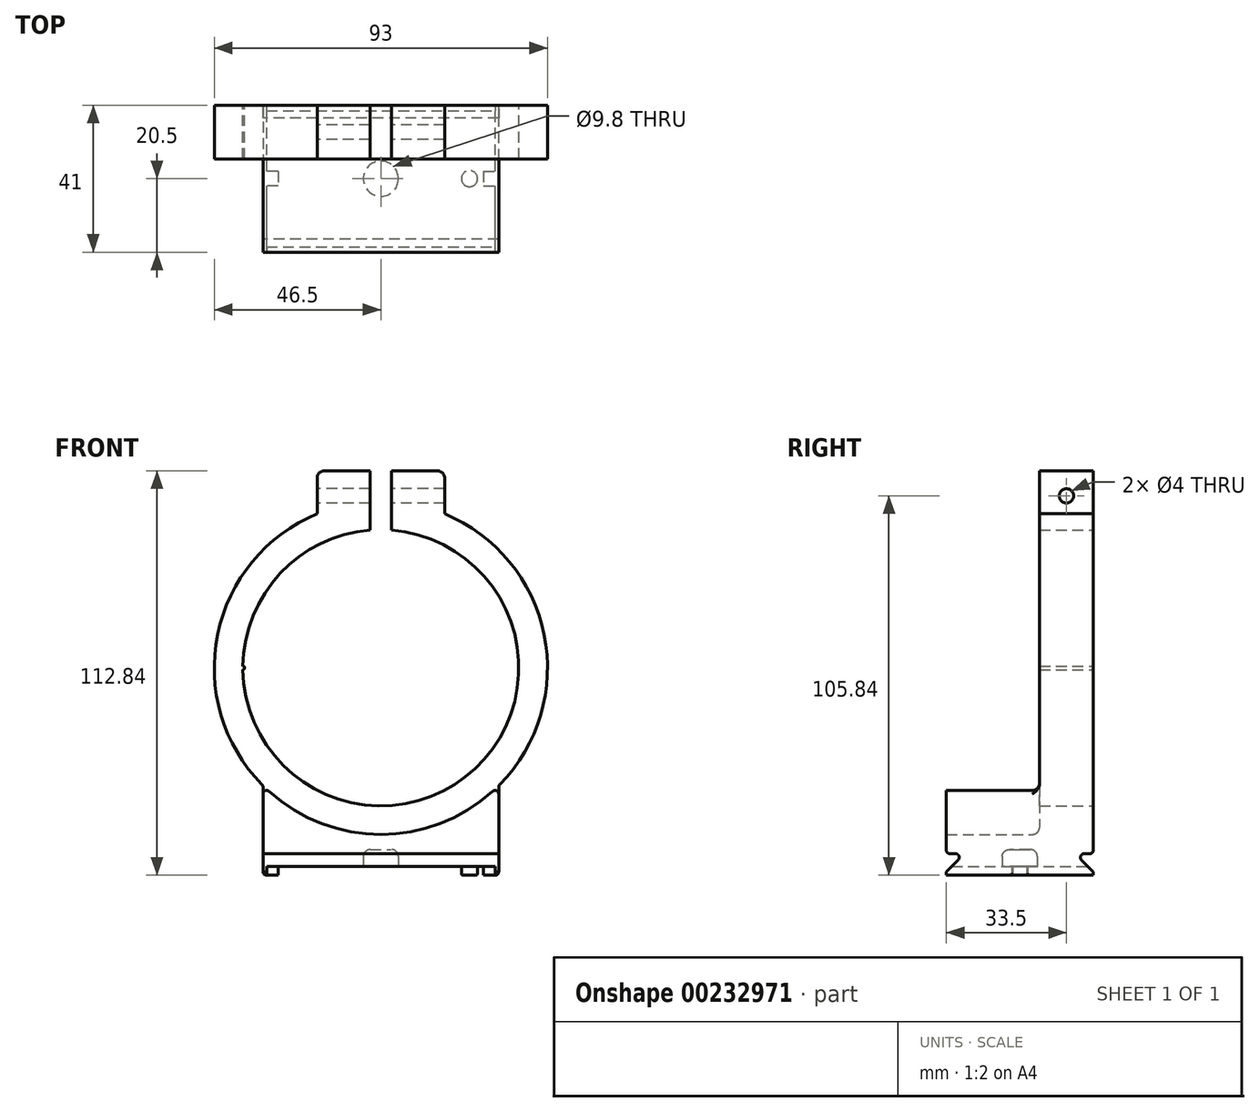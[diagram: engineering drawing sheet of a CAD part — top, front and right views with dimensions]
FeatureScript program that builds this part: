
annotation { "Feature Type Name" : "Feature", "Feature Type Description" : "" }
export const myFeature = defineFeature(function(context is Context, id is Id, definition is map)
    precondition{}
    {
        {
            var Q0;
            Q0=qCreatedBy(makeId("Front.planeOp"),FACE);
            var sketch = newSketch(context, id + "F0", { "sketchPlane" : qUnion([Q0])});
            skLineSegment(sketch, "E0", {"start": v(0, 0) * mm, "end": v(-32.88, -32.88) * mm, "construction": true});
            skLineSegment(sketch, "E1.MirrorCS", {"start": v(0, 0) * mm, "end": v(32.88, -32.88) * mm, "construction": true});
            skLineSegment(sketch, "E2", {"start": v(0, 0) * mm, "end": v(0, -46.5) * mm, "construction": true});
            skLineSegment(sketch, "E3.top", {"start": v(-32.88, -57.88) * mm, "end": v(32.88, -57.88) * mm});
            skLineSegment(sketch, "E3.left", {"start": v(-32.88, -32.88) * mm, "end": v(-32.88, -57.88) * mm});
            skLineSegment(sketch, "E3.right", {"start": v(32.88, -32.88) * mm, "end": v(32.88, -57.88) * mm});
            skLineSegment(sketch, "E4.MirrorCS", {"start": v(0, 0) * mm, "end": v(32.88, 32.88) * mm, "construction": true});
            skLineSegment(sketch, "E5.MirrorCS", {"start": v(0, 0) * mm, "end": v(-32.88, 32.88) * mm, "construction": true});
            skLineSegment(sketch, "E6", {"start": v(0, 0) * mm, "end": v(17.8, 42.96) * mm, "construction": true});
            skLineSegment(sketch, "E7.MirrorCS", {"start": v(0, 0) * mm, "end": v(-17.8, 42.96) * mm, "construction": true});
            skLineSegment(sketch, "E8.top", {"start": v(-15.8, 54.96) * mm, "end": v(-3, 54.96) * mm});
            skLineSegment(sketch, "E8.left", {"start": v(-17.8, 42.96) * mm, "end": v(-17.8, 52.96) * mm});
            skLineSegment(sketch, "E8.right", {"start": v(17.8, 42.96) * mm, "end": v(17.8, 52.96) * mm});
            skPoint(sketch, "E9.visualSharp", {"position": v(-17.8, 54.96) * mm});
            skArc(sketch, "E9.filletArc", {"start": v(-15.8, 54.96) * mm, "mid": v(-17.2, 54.37) * mm, "end": v(-17.8, 52.96) * mm});
            skPoint(sketch, "E10.visualSharp", {"position": v(17.8, 54.96) * mm});
            skArc(sketch, "E10.filletArc", {"start": v(17.8, 52.96) * mm, "mid": v(17.2, 54.37) * mm, "end": v(15.8, 54.96) * mm});
            skPoint(sketch, "E11", {"position": v(-3, 38.38) * mm});
            skPoint(sketch, "E12.MirrorP", {"position": v(3, 38.38) * mm});
            skLineSegment(sketch, "E13", {"start": v(-3, 38.38) * mm, "end": v(-3, 46.4) * mm});
            skLineSegment(sketch, "E14", {"start": v(3, 38.38) * mm, "end": v(3, 46.4) * mm});
            skLineSegment(sketch, "E15", {"start": v(0.05, 38.5) * mm, "end": v(0.05, 38.5) * mm});
            skArc(sketch, "E16", {"start": v(-3, 38.38) * mm, "mid": v(0, -38.5) * mm, "end": v(3, 38.38) * mm});
            skLineSegment(sketch, "E17", {"start": v(3, 54.96) * mm, "end": v(15.8, 54.96) * mm});
            skLineSegment(sketch, "E18", {"start": v(-3, 46.4) * mm, "end": v(-3, 54.96) * mm});
            skLineSegment(sketch, "E19", {"start": v(3, 46.4) * mm, "end": v(3, 54.96) * mm});
            skArc(sketch, "E20", {"start": v(-3, 46.4) * mm, "mid": v(0, -46.5) * mm, "end": v(3, 46.4) * mm});
            skArc(sketch, "E21", {"start": v(-38.5, -0.5) * mm, "mid": v(-38, 0) * mm, "end": v(-38.5, 0.5) * mm});
            skArc(sketch, "E22.MirrorCS", {"start": v(-0.5, -38.5) * mm, "mid": v(0, -38) * mm, "end": v(0.5, -38.5) * mm});
            skArc(sketch, "E23.MirrorCS", {"start": v(38.5, -0.5) * mm, "mid": v(38, 0) * mm, "end": v(38.5, 0.5) * mm});
            skSolve(sketch);
        }
        {
            var Q0;
            Q0=makeQuery(id+"F0.imprint","IMPRINT",FACE,{"disambiguationData":[TD([[makeQuery(id+"F0.imprint","IMPRINT",EDGE,{"derivedFrom":sQuery(id+"F0.wireOp",EDGE,"1u5II1qU-nMGl-KZTy-Vj3Y-kYBSh77GBjj7")}),-1.0]])]});
            var Q1;
            {var subQ0=sQuery(id+"F0.wireOp",EDGE,"E8.left");Q1=makeQuery(id+"F0.imprint","IMPRINT",FACE,{"disambiguationData":[TD([[makeQuery(id+"F0.imprint","IMPRINT",EDGE,{"derivedFrom":subQ0}),-1.0]])]});}
            var Q2;
            {var subQ0=sQuery(id+"F0.wireOp",EDGE,"E8.right");Q2=makeQuery(id+"F0.imprint","IMPRINT",FACE,{"disambiguationData":[TD([[makeQuery(id+"F0.imprint","IMPRINT",EDGE,{"derivedFrom":subQ0}),1.0]])]});}
            var Q3;
            {var subQ2=sQuery(id+"F0.wireOp",EDGE,"E13");Q3=makeQuery(id+"F0.imprint","IMPRINT",FACE,{"disambiguationData":[TD([[makeQuery(id+"F0.imprint","IMPRINT",EDGE,{"derivedFrom":subQ2}),1.0]])]});}
            var Q4;
            {var subQ0=sQuery(id+"F0.wireOp",EDGE,"E21");Q4=makeQuery(id+"F0.imprint","IMPRINT",FACE,{"disambiguationData":[TD([[makeQuery(id+"F0.imprint","IMPRINT",EDGE,{"derivedFrom":subQ0}),1.0]])]});}
            var Q5;
            {var subQ0=sQuery(id+"F0.wireOp",EDGE,"E22.MirrorCS");Q5=makeQuery(id+"F0.imprint","IMPRINT",FACE,{"disambiguationData":[TD([[makeQuery(id+"F0.imprint","IMPRINT",EDGE,{"derivedFrom":subQ0}),-1.0]])]});}
            var Q6;
            {var subQ0=sQuery(id+"F0.wireOp",EDGE,"E23.MirrorCS");Q6=makeQuery(id+"F0.imprint","IMPRINT",FACE,{"disambiguationData":[TD([[makeQuery(id+"F0.imprint","IMPRINT",EDGE,{"derivedFrom":subQ0}),-1.0]])]});}
            var Q7;
            Q7=makeQuery(id+"F0.imprint","IMPRINT",FACE,{"disambiguationData":[TD([[makeQuery(id+"F0.imprint","IMPRINT",EDGE,{"derivedFrom":sQuery(id+"F0.wireOp",EDGE,"E3.top")}),1.0]])]});
            extrude(context, id + "F1", {"entities" : qUnion([Q0, Q1, Q2, Q3, Q4, Q5, Q6, Q7]), "endBound" : BoundingType.SYMMETRIC, "depth" : 15 * mm});
        }
        {
            var Q0;
            Q0=makeQuery(id+"F1.opExtrude","SWEPT_FACE",FACE,{"disambiguationData":[OSD([sQuery(id+"F0.wireOp",EDGE,"E8.left")])]});
            var sketch = newSketch(context, id + "F2", { "sketchPlane" : qUnion([Q0])});
            skPoint(sketch, "E24", {"position": v(0, 47.96) * mm});
            skPoint(sketch, "E24.positionSnap0", {"position": v(-7.5, 47.96) * mm});
            skPoint(sketch, "E25", {"position": v(7.5, 47.96) * mm});
            skLineSegment(sketch, "E26", {"start": v(-7.5, 47.96) * mm, "end": v(7.5, 47.96) * mm, "construction": true});
            skSolve(sketch);
        }
        {
            var Q0;
            Q0=sQuery(id+"F2.wireOp",VERTEX,"E24");
            var Q1;
            Q1=makeQuery(id+"F1.opExtrude","SWEPT_BODY",BODY,{"disambiguationData":[OSD([sQuery(id+"F0.wireOp",EDGE,"E3.top"),sQuery(id+"F0.wireOp",EDGE,"E3.left"),sQuery(id+"F0.wireOp",EDGE,"E3.right"),sQuery(id+"F0.wireOp",EDGE,"E8.top"),sQuery(id+"F0.wireOp",EDGE,"E8.left"),sQuery(id+"F0.wireOp",EDGE,"E8.right"),sQuery(id+"F0.wireOp",EDGE,"E9.filletArc"),sQuery(id+"F0.wireOp",EDGE,"E10.filletArc"),sQuery(id+"F0.wireOp",EDGE,"E13"),sQuery(id+"F0.wireOp",EDGE,"E14"),sQuery(id+"F0.wireOp",EDGE,"E16"),sQuery(id+"F0.wireOp",EDGE,"E17"),sQuery(id+"F0.wireOp",EDGE,"E18"),sQuery(id+"F0.wireOp",EDGE,"E19"),sQuery(id+"F0.wireOp",EDGE,"E20")])]});
            hole(context, id + "F3", {"style" : HoleStyle.SIMPLE, "endStyle" : HoleEndStyle.THROUGH, "holeDiameter" : 4 * mm, "locations" : qUnion([Q0]), "scope" : qUnion([Q1]), "isTappedThrough" : true});
        }
        {
            var Q0;
            Q0=makeQuery(id+"F0.imprint","IMPRINT",FACE,{"disambiguationData":[TD([[makeQuery(id+"F0.imprint","IMPRINT",EDGE,{"derivedFrom":sQuery(id+"F0.wireOp",EDGE,"E3.top")}),1.0]])]});
            extrude(context, id + "F4", {"entities" : qUnion([Q0]), "operationType" : NewBodyOperationType.ADD, "depth" : 33.5 * mm, "hasSecondDirection" : true, "secondDirectionOppositeDirection" : true, "secondDirectionDepth" : 7.5 * mm});
        }
        {
            var Q0;
            Q0=makeQuery(id+"F1.opExtrude","SWEPT_FACE",FACE,{"disambiguationData":[OSD([sQuery(id+"F0.wireOp",EDGE,"E3.right")])]});
            var sketch = newSketch(context, id + "F5", { "sketchPlane" : qUnion([Q0])});
            skLineSegment(sketch, "E27", {"start": v(-33.5, -57.88) * mm, "end": v(7.5, -57.88) * mm, "construction": true});
            skLineSegment(sketch, "E28", {"start": v(-33.5, -56.88) * mm, "end": v(-33.5, -51.88) * mm});
            skLineSegment(sketch, "E29", {"start": v(-33.5, -51.88) * mm, "end": v(-28.5, -51.88) * mm});
            skLineSegment(sketch, "E30", {"start": v(-28.5, -51.88) * mm, "end": v(-33.5, -56.88) * mm});
            skLineSegment(sketch, "E31", {"start": v(7.5, -56.88) * mm, "end": v(7.5, -51.88) * mm});
            skLineSegment(sketch, "E32", {"start": v(7.5, -51.88) * mm, "end": v(2.5, -51.88) * mm});
            skLineSegment(sketch, "E33", {"start": v(2.5, -51.88) * mm, "end": v(7.5, -56.88) * mm});
            skLineSegment(sketch, "E34", {"start": v(7.5, -51.88) * mm, "end": v(7.5, -56.88) * mm});
            skSolve(sketch);
        }
        {
            var Q0;
            Q0=makeQuery(id+"F5.imprint","IMPRINT",FACE,{"disambiguationData":[TD([[makeQuery(id+"F5.imprint","IMPRINT",EDGE,{"derivedFrom":sQuery(id+"F5.wireOp",EDGE,"E28")}),1.0]])]});
            var Q1;
            Q1=makeQuery(id+"F5.imprint","IMPRINT",FACE,{"disambiguationData":[TD([[makeQuery(id+"F5.imprint","IMPRINT",EDGE,{"derivedFrom":sQuery(id+"F5.wireOp",EDGE,"E32")}),1.0]])]});
            extrude(context, id + "F6", {"entities" : qUnion([Q0, Q1]), "operationType" : NewBodyOperationType.REMOVE, "endBound" : BoundingType.THROUGH_ALL, "oppositeDirection" : true, "depth" : 25 * mm});
        }
        {
            var Q0;
            Q0=makeQuery(id+"F6.boolean.opBoolean","COPY",EDGE,{"derivedFrom":makeQuery(id+"F6.opExtrude","SWEPT_EDGE",EDGE,{"disambiguationData":[OSD([sQuery(id+"F0.wireOp",EDGE,"E3.right"),sQuery(id+"F5.wireOp",EDGE,"E28"),sQuery(id+"F5.wireOp",EDGE,"E29")])]})});
            var Q1;
            Q1=makeQuery(id+"F6.boolean.opBoolean","COPY",EDGE,{"derivedFrom":makeQuery(id+"F6.opExtrude","SWEPT_EDGE",EDGE,{"disambiguationData":[OSD([sQuery(id+"F5.wireOp",EDGE,"E29"),sQuery(id+"F5.wireOp",EDGE,"E30")])]})});
            var Q2;
            Q2=makeQuery(id+"F6.boolean.opBoolean","COPY",EDGE,{"derivedFrom":makeQuery(id+"F6.opExtrude","SWEPT_EDGE",EDGE,{"disambiguationData":[OSD([sQuery(id+"F5.wireOp",EDGE,"E32"),sQuery(id+"F5.wireOp",EDGE,"E33")])]})});
            var Q3;
            Q3=makeQuery(id+"F6.boolean.opBoolean","COPY",EDGE,{"derivedFrom":makeQuery(id+"F6.opExtrude","SWEPT_EDGE",EDGE,{"disambiguationData":[OSD([sQuery(id+"F0.wireOp",EDGE,"E3.right"),sQuery(id+"F5.wireOp",EDGE,"E32"),sQuery(id+"F5.wireOp",EDGE,"E34")])]})});
            fillet(context, id + "F7", {"entities" : qUnion([Q0, Q1, Q2, Q3]), "radius" : 1 * mm, "tangentPropagation" : true, "allowEdgeOverflow" : false});
        }
        {
            var Q0;
            Q0=makeQuery(id+"F4.opExtrude","SWEPT_EDGE",EDGE,{"disambiguationData":[OSD([sQuery(id+"F10VlHSy7CHH0IY_1.wireOp",EDGE,"xWeDCezv-Av9h-x3vl-Ufey-5V87kZvHZ6QT"),sQuery(id+"F10VlHSy7CHH0IY_1.wireOp",EDGE,"y1Gu3GTH-5JIg-t1sE-E9Gf-zWUJNM3WsVzs")])]});
            var Q1;
            Q1=makeQuery(id+"F4.opExtrude","SWEPT_EDGE",EDGE,{"disambiguationData":[OSD([sQuery(id+"F10VlHSy7CHH0IY_1.wireOp",EDGE,"y1Gu3GTH-5JIg-t1sE-E9Gf-zWUJNM3WsVzs"),sQuery(id+"F10VlHSy7CHH0IY_1.wireOp",EDGE,"puxxrOXx-If6v-emkU-wFuk-THnEcJOJJWbn")])]});
            var Q2;
            {var subQ0=sQuery(id+"F0.wireOp",EDGE,"E3.left");var subQ1=sQuery(id+"F0.wireOp",EDGE,"E3.top");Q2=makeQuery(id+"F4.boolean.opBoolean","MERGE",EDGE,{"derivedFrom":[makeQuery(id+"F1.opExtrude","SWEPT_EDGE",EDGE,{"disambiguationData":[OSD([subQ1,subQ0])]}),makeQuery(id+"F4.opExtrude","SWEPT_EDGE",EDGE,{"disambiguationData":[OSD([subQ1,subQ0])]})]});}
            var Q3;
            {var subQ0=sQuery(id+"F0.wireOp",EDGE,"E3.right");var subQ1=sQuery(id+"F0.wireOp",EDGE,"E3.top");Q3=makeQuery(id+"F4.boolean.opBoolean","MERGE",EDGE,{"derivedFrom":[makeQuery(id+"F1.opExtrude","SWEPT_EDGE",EDGE,{"disambiguationData":[OSD([subQ1,subQ0])]}),makeQuery(id+"F4.opExtrude","SWEPT_EDGE",EDGE,{"disambiguationData":[OSD([subQ1,subQ0])]})]});}
            fillet(context, id + "F8", {"entities" : qUnion([Q0, Q1, Q2, Q3]), "radius" : 1 * mm, "tangentPropagation" : true, "allowEdgeOverflow" : false});
        }
        {
            var Q0;
            Q0=makeQuery(id+"F4.opExtrude","SWEPT_EDGE",EDGE,{"disambiguationData":[OSD([sQuery(id+"F0.wireOp",EDGE,"E3.left"),sQuery(id+"F0.wireOp",EDGE,"E20")])]});
            var Q1;
            Q1=makeQuery(id+"F4.opExtrude","SWEPT_EDGE",EDGE,{"disambiguationData":[OSD([sQuery(id+"F0.wireOp",EDGE,"E3.right"),sQuery(id+"F0.wireOp",EDGE,"E20")])]});
            fillet(context, id + "F9", {"entities" : qUnion([Q0, Q1]), "radius" : 1 * mm, "tangentPropagation" : true, "allowEdgeOverflow" : false});
        }
        {
            var Q0;
            {var subQ0=sQuery(id+"F0.wireOp",EDGE,"E20");Q0=makeQuery(id+"F4.boolean.opBoolean","INTERSECT",EDGE,{"derivedFrom":[makeQuery(id+"F1.opExtrude","CAP_FACE",FACE,{"disambiguationData":[OSD([sQuery(id+"F0.wireOp",EDGE,"E3.top"),sQuery(id+"F0.wireOp",EDGE,"E3.left"),sQuery(id+"F0.wireOp",EDGE,"E3.right"),sQuery(id+"F0.wireOp",EDGE,"E8.top"),sQuery(id+"F0.wireOp",EDGE,"E8.left"),sQuery(id+"F0.wireOp",EDGE,"E8.right"),sQuery(id+"F0.wireOp",EDGE,"E9.filletArc"),sQuery(id+"F0.wireOp",EDGE,"E10.filletArc"),sQuery(id+"F0.wireOp",EDGE,"E13"),sQuery(id+"F0.wireOp",EDGE,"E14"),sQuery(id+"F0.wireOp",EDGE,"E16"),sQuery(id+"F0.wireOp",EDGE,"E17"),sQuery(id+"F0.wireOp",EDGE,"E18"),sQuery(id+"F0.wireOp",EDGE,"E19"),subQ0,sQuery(id+"F0.wireOp",EDGE,"E21"),sQuery(id+"F0.wireOp",EDGE,"E22.MirrorCS"),sQuery(id+"F0.wireOp",EDGE,"E23.MirrorCS")])],"isStart":false}),makeQuery(id+"F4.opExtrude","SWEPT_FACE",FACE,{"disambiguationData":[OSD([subQ0])]})]});}
            fillet(context, id + "F10", {"entities" : qUnion([Q0]), "radius" : 2 * mm, "tangentPropagation" : true, "allowEdgeOverflow" : false});
        }
        {
            var Q0;
            Q0=makeQuery(id+"F1.opExtrude","SWEPT_EDGE",EDGE,{"disambiguationData":[OSD([sQuery(id+"F0.wireOp",EDGE,"E3.right"),sQuery(id+"F0.wireOp",EDGE,"E20")])]});
            var Q1;
            Q1=makeQuery(id+"F1.opExtrude","SWEPT_EDGE",EDGE,{"disambiguationData":[OSD([sQuery(id+"F0.wireOp",EDGE,"E3.left"),sQuery(id+"F0.wireOp",EDGE,"E20")])]});
            fillet(context, id + "F11", {"entities" : qUnion([Q0, Q1]), "radius" : 1 * mm, "tangentPropagation" : true, "allowEdgeOverflow" : false});
        }
        {
            var Q0;
            {var subQ0=sQuery(id+"F0.wireOp",EDGE,"E3.top");Q0=makeQuery(id+"F4.boolean.opBoolean","MERGE",FACE,{"derivedFrom":[makeQuery(id+"F1.opExtrude","SWEPT_FACE",FACE,{"disambiguationData":[OSD([subQ0])]}),makeQuery(id+"F4.opExtrude","SWEPT_FACE",FACE,{"disambiguationData":[OSD([subQ0])]})]});}
            var sketch = newSketch(context, id + "F12", { "sketchPlane" : qUnion([Q0])});
            skLineSegment(sketch, "E35", {"start": v(-32.72, 13) * mm, "end": v(32.95, 13) * mm, "construction": true});
            skPoint(sketch, "E35.startSnap0", {"position": v(-31.88, 13) * mm});
            skCircle(sketch, "E36", {"center": v(-24.72, 13) * mm, "radius": 2.25 * mm});
            skCircle(sketch, "E37.MirrorC", {"center": v(24.72, 13) * mm, "radius": 2.25 * mm});
            skCircle(sketch, "E38", {"center": v(0, 13) * mm, "radius": 4.9 * mm});
            skPoint(sketch, "E38.centerSnap0", {"position": v(0.11, 13) * mm});
            skLineSegment(sketch, "E39.bottom", {"start": v(28.67, 11) * mm, "end": v(37.23, 11) * mm});
            skLineSegment(sketch, "E39.top", {"start": v(28.67, 15) * mm, "end": v(37.23, 15) * mm});
            skLineSegment(sketch, "E39.left", {"start": v(28.67, 11) * mm, "end": v(28.67, 15) * mm});
            skLineSegment(sketch, "E39.right", {"start": v(37.23, 11) * mm, "end": v(37.23, 15) * mm});
            skPoint(sketch, "E39.middle", {"position": v(32.95, 13) * mm});
            skLineSegment(sketch, "E40.MirrorCS", {"start": v(-37.23, 11) * mm, "end": v(-37.23, 15) * mm});
            skLineSegment(sketch, "E41.MirrorCS", {"start": v(-28.67, 11) * mm, "end": v(-37.23, 11) * mm});
            skLineSegment(sketch, "E42.MirrorCS", {"start": v(-28.67, 15) * mm, "end": v(-37.23, 15) * mm});
            skLineSegment(sketch, "E43.MirrorCS", {"start": v(-28.67, 11) * mm, "end": v(-28.67, 15) * mm});
            skSolve(sketch);
        }
        {
            var Q0;
            Q0=makeQuery(id+"F12.imprint","IMPRINT",FACE,{"disambiguationData":[TD([[makeQuery(id+"F12.imprint","IMPRINT",EDGE,{"derivedFrom":sQuery(id+"F12.wireOp",EDGE,"E36")}),1.0]])]});
            var Q1;
            Q1=makeQuery(id+"F12.imprint","IMPRINT",FACE,{"disambiguationData":[TD([[makeQuery(id+"F12.imprint","IMPRINT",EDGE,{"derivedFrom":sQuery(id+"F12.wireOp",EDGE,"E37.MirrorC")}),-1.0]])]});
            extrude(context, id + "F13", {"entities" : qUnion([Q0, Q1]), "operationType" : NewBodyOperationType.REMOVE, "oppositeDirection" : true, "depth" : 2.5 * mm});
        }
        {
            var Q0;
            Q0=makeQuery(id+"F13.boolean.opBoolean","COPY",FACE,{"derivedFrom":makeQuery(id+"F13.opExtrude","CAP_FACE",FACE,{"disambiguationData":[OSD([sQuery(id+"F12.wireOp",EDGE,"E36")])],"isStart":false})});
            var Q1;
            Q1=makeQuery(id+"F13.boolean.opBoolean","COPY",EDGE,{"derivedFrom":makeQuery(id+"F13.opExtrude","CAP_EDGE",EDGE,{"disambiguationData":[OSD([sQuery(id+"F12.wireOp",EDGE,"E37.MirrorC")])],"isStart":true})});
            fillet(context, id + "F14", {"entities" : qUnion([Q0, Q1]), "radius" : 0.5 * mm, "tangentPropagation" : true, "allowEdgeOverflow" : false});
        }
        {
            var Q0;
            Q0=makeQuery(id+"F12.imprint","IMPRINT",FACE,{"disambiguationData":[TD([[makeQuery(id+"F12.imprint","IMPRINT",EDGE,{"derivedFrom":sQuery(id+"F12.wireOp",EDGE,"E38")}),1.0]])]});
            extrude(context, id + "F15", {"entities" : qUnion([Q0]), "operationType" : NewBodyOperationType.REMOVE, "oppositeDirection" : true, "depth" : 7.2 * mm});
        }
        {
            var Q0;
            Q0=makeQuery(id+"F15.boolean.opBoolean","COPY",FACE,{"derivedFrom":makeQuery(id+"F15.opExtrude","CAP_FACE",FACE,{"disambiguationData":[OSD([sQuery(id+"F12.wireOp",EDGE,"E38")])],"isStart":false})});
            fillet(context, id + "F16", {"entities" : qUnion([Q0]), "radius" : 2 * mm, "tangentPropagation" : true, "allowEdgeOverflow" : false});
        }
    });
